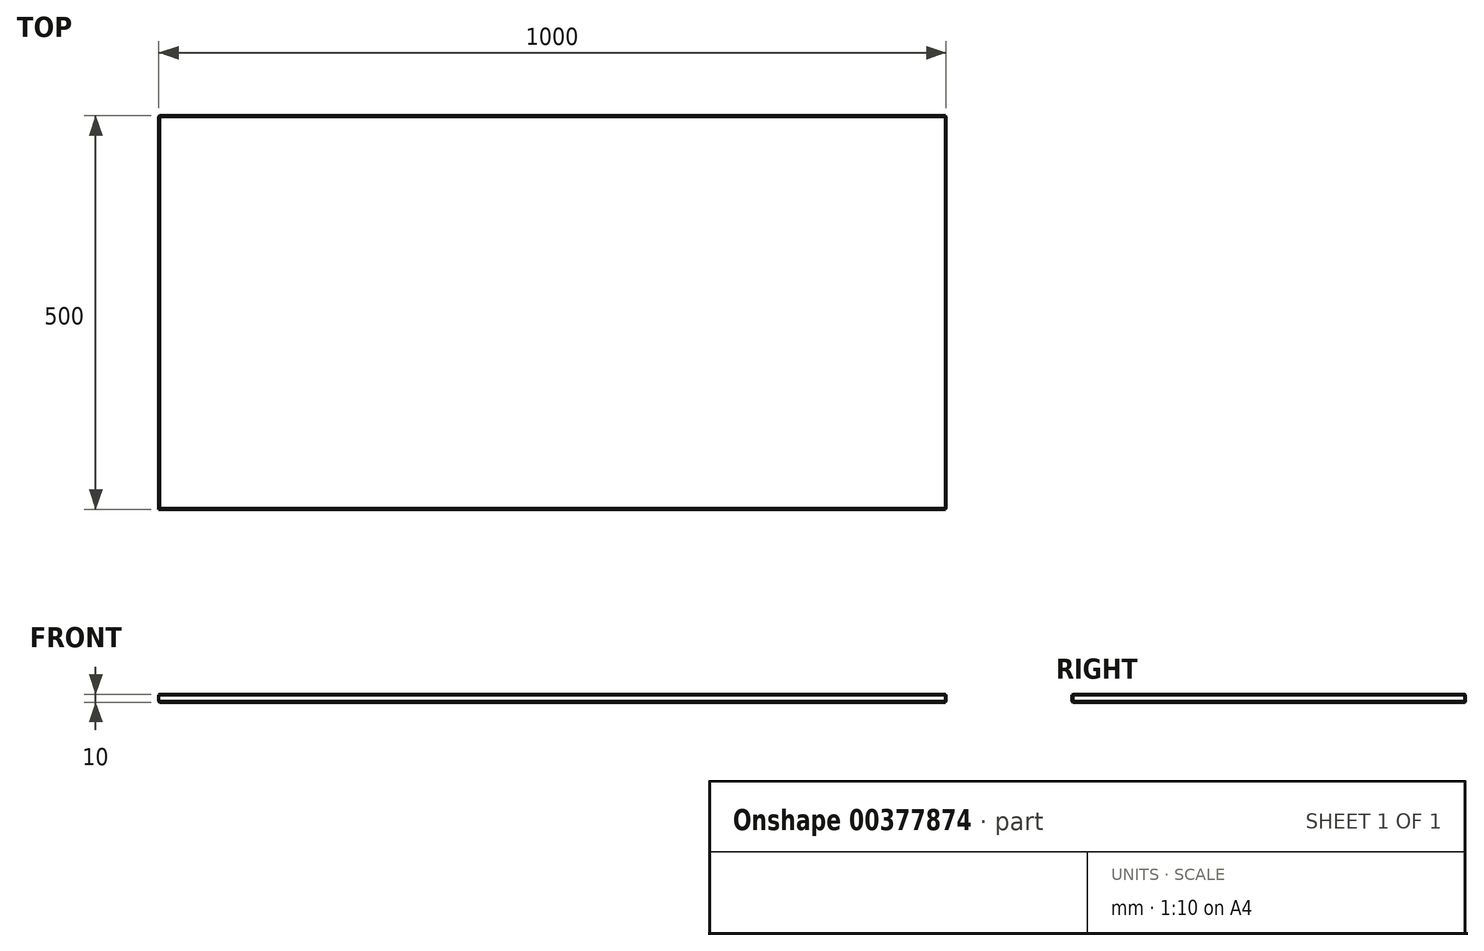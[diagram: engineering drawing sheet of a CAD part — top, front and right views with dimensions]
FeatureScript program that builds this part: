
annotation { "Feature Type Name" : "Feature", "Feature Type Description" : "" }
export const myFeature = defineFeature(function(context is Context, id is Id, definition is map)
    precondition{}
    {
        {
            var Q0;
            Q0=qCreatedBy(makeId("Top.planeOp"),FACE);
            var sketch = newSketch(context, id + "F0", { "sketchPlane" : qUnion([Q0])});
            skLineSegment(sketch, "E0.bottom", {"start": v(500, 250) * mm, "end": v(-500, 250) * mm});
            skLineSegment(sketch, "E0.top", {"start": v(500, -250) * mm, "end": v(-500, -250) * mm});
            skLineSegment(sketch, "E0.left", {"start": v(500, 250) * mm, "end": v(500, -250) * mm});
            skLineSegment(sketch, "E0.right", {"start": v(-500, 250) * mm, "end": v(-500, -250) * mm});
            skPoint(sketch, "E0.middle", {"position": v(0, 0) * mm});
            skSolve(sketch);
        }
        {
            var Q0;
            Q0 = qSketchRegion(id + "F0", true);
            var Q1;
            Q1=makeQuery(id+"F0.imprint","IMPRINT",FACE,{"disambiguationData":[TD([[makeQuery(id+"F0.imprint","IMPRINT",EDGE,{"derivedFrom":sQuery(id+"F0.wireOp",EDGE,"E0.bottom")}),1.0]])]});
            extrude(context, id + "F1", {"entities" : qUnion([Q0, Q1]), "endBound" : BoundingType.SYMMETRIC, "depth" : 10 * mm});
        }
        {
            var Q0;
            Q0=makeQuery(id+"F1.opExtrude","CAP_EDGE",EDGE,{"disambiguationData":[OSD([sQuery(id+"F0.wireOp",EDGE,"E0.bottom")])],"isStart":false});
            chamfer(context, id + "F2", {"entities" : qUnion([Q0]), "width" : 1 * mm, "tangentPropagation" : true});
        }
        {
            var Q0;
            Q0=makeQuery(id+"F1.opExtrude","CAP_EDGE",EDGE,{"disambiguationData":[OSD([sQuery(id+"F0.wireOp",EDGE,"E0.left")])],"isStart":false});
            chamfer(context, id + "F3", {"entities" : qUnion([Q0]), "width" : 1 * mm, "tangentPropagation" : true});
        }
        {
            var Q0;
            Q0=makeQuery(id+"F1.opExtrude","CAP_EDGE",EDGE,{"disambiguationData":[OSD([sQuery(id+"F0.wireOp",EDGE,"E0.left")])],"isStart":true});
            chamfer(context, id + "F4", {"entities" : qUnion([Q0]), "width" : 1 * mm, "tangentPropagation" : true});
        }
        {
            var Q0;
            Q0=makeQuery(id+"F1.opExtrude","SWEPT_EDGE",EDGE,{"disambiguationData":[OSD([sQuery(id+"F0.wireOp",EDGE,"E0.bottom"),sQuery(id+"F0.wireOp",EDGE,"E0.left")])]});
            chamfer(context, id + "F5", {"entities" : qUnion([Q0]), "width" : 1 * mm, "tangentPropagation" : true});
        }
        {
            var Q0;
            Q0=makeQuery(id+"F1.opExtrude","CAP_EDGE",EDGE,{"disambiguationData":[OSD([sQuery(id+"F0.wireOp",EDGE,"E0.bottom")])],"isStart":true});
            chamfer(context, id + "F6", {"entities" : qUnion([Q0]), "width" : 1 * mm, "tangentPropagation" : true});
        }
        {
            var Q0;
            Q0=makeQuery(id+"F1.opExtrude","CAP_EDGE",EDGE,{"disambiguationData":[OSD([sQuery(id+"F0.wireOp",EDGE,"E0.top")])],"isStart":false});
            var Q1;
            Q1=makeQuery(id+"F1.opExtrude","CAP_EDGE",EDGE,{"disambiguationData":[OSD([sQuery(id+"F0.wireOp",EDGE,"E0.top")])],"isStart":true});
            var Q2;
            Q2=makeQuery(id+"F1.opExtrude","SWEPT_EDGE",EDGE,{"disambiguationData":[OSD([sQuery(id+"F0.wireOp",EDGE,"E0.top"),sQuery(id+"F0.wireOp",EDGE,"E0.left")])]});
            chamfer(context, id + "F7", {"entities" : qUnion([Q0, Q1, Q2]), "width" : 1 * mm, "tangentPropagation" : true});
        }
        {
            var Q0;
            Q0=makeQuery(id+"F1.opExtrude","SWEPT_EDGE",EDGE,{"disambiguationData":[OSD([sQuery(id+"F0.wireOp",EDGE,"E0.bottom"),sQuery(id+"F0.wireOp",EDGE,"E0.right")])]});
            var Q1;
            Q1=makeQuery(id+"F1.opExtrude","CAP_EDGE",EDGE,{"disambiguationData":[OSD([sQuery(id+"F0.wireOp",EDGE,"E0.right")])],"isStart":false});
            var Q2;
            Q2=makeQuery(id+"F1.opExtrude","CAP_EDGE",EDGE,{"disambiguationData":[OSD([sQuery(id+"F0.wireOp",EDGE,"E0.right")])],"isStart":true});
            chamfer(context, id + "F8", {"entities" : qUnion([Q0, Q1, Q2]), "width" : 1 * mm, "tangentPropagation" : true});
        }
    });
